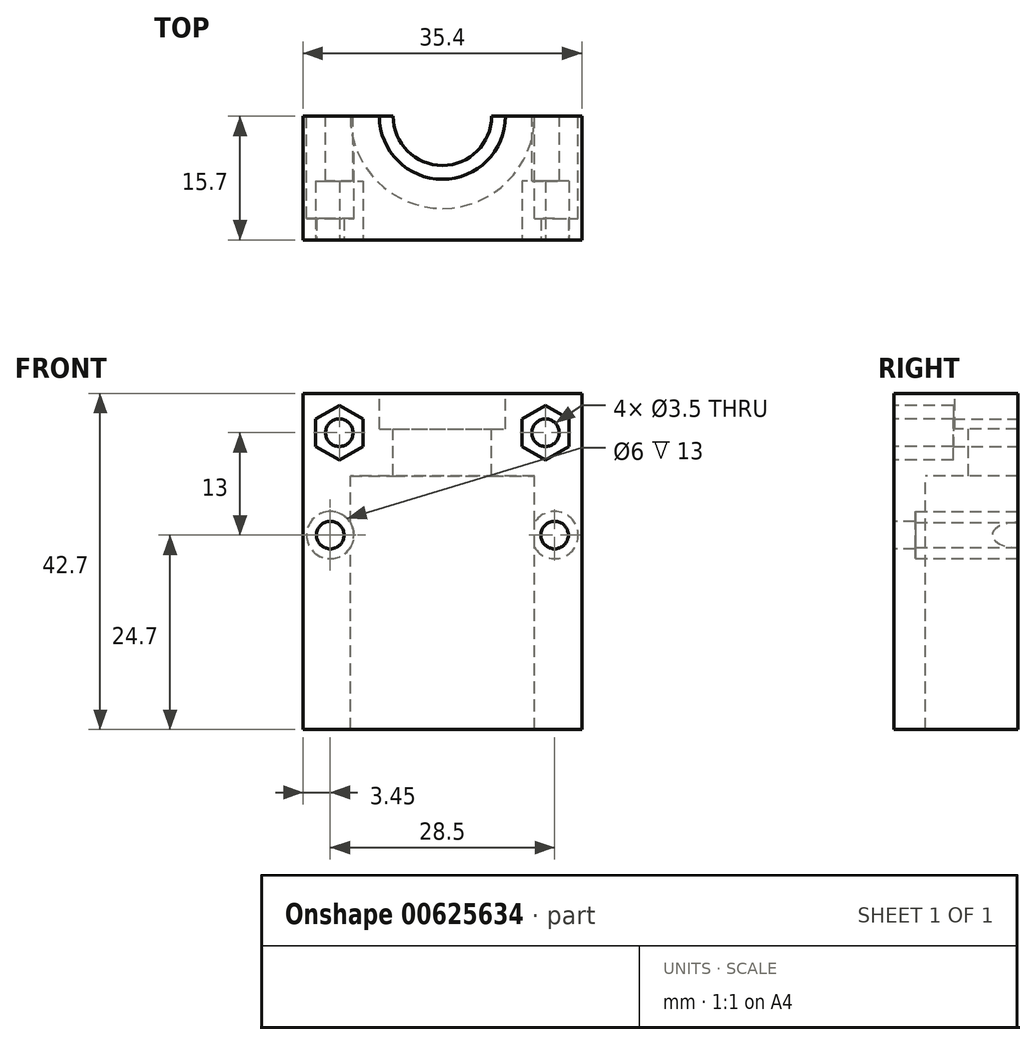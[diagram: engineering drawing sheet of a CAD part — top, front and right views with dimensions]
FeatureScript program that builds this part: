
annotation { "Feature Type Name" : "Feature", "Feature Type Description" : "" }
export const myFeature = defineFeature(function(context is Context, id is Id, definition is map)
    precondition{}
    {
        {
            var Q0;
            Q0=qCreatedBy(makeId("Top.planeOp"),FACE);
            var sketch = newSketch(context, id + "F0", { "sketchPlane" : qUnion([Q0])});
            skLineSegment(sketch, "E0.bottom", {"start": v(0, 0) * mm, "end": v(35.4, 0) * mm});
            skLineSegment(sketch, "E0.top", {"start": v(0, 15.7) * mm, "end": v(7.2, 15.7) * mm});
            skLineSegment(sketch, "E0.left", {"start": v(0, 0) * mm, "end": v(0, 15.7) * mm});
            skLineSegment(sketch, "E0.right", {"start": v(35.4, 0) * mm, "end": v(35.4, 15.7) * mm});
            skLineSegment(sketch, "E1.trimOffspring", {"start": v(23.2, 15.7) * mm, "end": v(35.4, 15.7) * mm});
            skLineSegment(sketch, "E2", {"start": v(7.2, 15.7) * mm, "end": v(23.2, 15.7) * mm});
            skSolve(sketch);
        }
        {
            var Q0;
            Q0=makeQuery(id+"F0.imprint","IMPRINT",FACE,{"disambiguationData":[TD([[makeQuery(id+"F0.imprint","IMPRINT",EDGE,{"derivedFrom":sQuery(id+"F0.wireOp",EDGE,"E0.bottom")}),1.0]])]});
            extrude(context, id + "F1", {"entities" : qUnion([Q0]), "depth" : 42.7 * mm, "offsetDistance" : 25 * mm});
        }
        {
            var Q0;
            Q0=makeQuery(id+"F1.opExtrude","CAP_FACE",FACE,{"disambiguationData":[OSD([sQuery(id+"F0.wireOp",EDGE,"E0.bottom"),sQuery(id+"F0.wireOp",EDGE,"E0.top"),sQuery(id+"F0.wireOp",EDGE,"E0.left"),sQuery(id+"F0.wireOp",EDGE,"E0.right"),sQuery(id+"F0.wireOp",EDGE,"E1.trimOffspring"),sQuery(id+"F0.wireOp",EDGE,"E2")])],"isStart":false});
            var sketch = newSketch(context, id + "F2", { "sketchPlane" : qUnion([Q0])});
            skCircle(sketch, "E3", {"center": v(17.7, 15.7) * mm, "radius": 8 * mm});
            skSolve(sketch);
        }
        {
            var Q0;
            {var subQ0=sQuery(id+"F2.wireOp",EDGE,"E3");var subQ1=makeQuery(id+"F1.opExtrude","CAP_EDGE",EDGE,{"disambiguationData":[OSD([sQuery(id+"F0.wireOp",EDGE,"E0.top"),sQuery(id+"F0.wireOp",EDGE,"E1.trimOffspring"),sQuery(id+"F0.wireOp",EDGE,"E2")])],"isStart":false});var subQ2=makeQuery(id+"F2.imprint","INTERSECT",VERTEX,{"disambiguationData":[OD(0.0)],"derivedFrom":[subQ1,subQ0]});Q0=makeQuery(id+"F2.imprint","IMPRINT",FACE,{"disambiguationData":[TD([[makeQuery(id+"F2.imprint","IMPRINT",EDGE,{"disambiguationData":[TD([[subQ2,-1.0]])],"derivedFrom":subQ0}),1.0]])]});}
            extrude(context, id + "F3", {"entities" : qUnion([Q0]), "operationType" : NewBodyOperationType.REMOVE, "oppositeDirection" : true, "depth" : 4.5 * mm, "offsetDistance" : 25 * mm});
        }
        {
            var Q0;
            Q0=makeQuery(id+"F3.boolean.opBoolean","COPY",FACE,{"derivedFrom":makeQuery(id+"F3.opExtrude","CAP_FACE",FACE,{"disambiguationData":[OSD([sQuery(id+"F0.wireOp",EDGE,"E0.top"),sQuery(id+"F0.wireOp",EDGE,"E1.trimOffspring"),sQuery(id+"F0.wireOp",EDGE,"E2"),sQuery(id+"F2.wireOp",EDGE,"E3")])],"isStart":false})});
            var sketch = newSketch(context, id + "F4", { "sketchPlane" : qUnion([Q0])});
            skPoint(sketch, "E4.center.orphan", {"position": v(17.7, 15.7) * mm});
            skCircle(sketch, "E5", {"center": v(17.7, 15.7) * mm, "radius": 6.25 * mm});
            skSolve(sketch);
        }
        {
            var Q0;
            {var subQ0=sQuery(id+"F4.wireOp",EDGE,"E5");var subQ1=makeQuery(id+"F3.boolean.opBoolean","COPY",EDGE,{"derivedFrom":makeQuery(id+"F3.opExtrude","CAP_EDGE",EDGE,{"disambiguationData":[OSD([sQuery(id+"F0.wireOp",EDGE,"E0.top"),sQuery(id+"F0.wireOp",EDGE,"E1.trimOffspring"),sQuery(id+"F0.wireOp",EDGE,"E2")])],"isStart":false})});var subQ2=makeQuery(id+"F4.imprint","INTERSECT",VERTEX,{"disambiguationData":[OD(0.0)],"derivedFrom":[subQ1,subQ0]});Q0=makeQuery(id+"F4.imprint","IMPRINT",FACE,{"disambiguationData":[TD([[makeQuery(id+"F4.imprint","IMPRINT",EDGE,{"disambiguationData":[TD([[subQ2,-1.0]])],"derivedFrom":subQ0}),1.0]])]});}
            extrude(context, id + "F5", {"entities" : qUnion([Q0]), "operationType" : NewBodyOperationType.REMOVE, "oppositeDirection" : true, "depth" : 6 * mm, "offsetDistance" : 25 * mm});
        }
        {
            var Q0;
            Q0=makeQuery(id+"F5.boolean.opBoolean","COPY",FACE,{"derivedFrom":makeQuery(id+"F5.opExtrude","CAP_FACE",FACE,{"disambiguationData":[OSD([sQuery(id+"F0.wireOp",EDGE,"E0.top"),sQuery(id+"F0.wireOp",EDGE,"E1.trimOffspring"),sQuery(id+"F0.wireOp",EDGE,"E2"),sQuery(id+"F4.wireOp",EDGE,"E5")])],"isStart":false})});
            var sketch = newSketch(context, id + "F6", { "sketchPlane" : qUnion([Q0])});
            skCircle(sketch, "E6", {"center": v(17.7, 15.7) * mm, "radius": 8 * mm});
            skSolve(sketch);
        }
        {
            var Q0;
            Q0 = qSketchRegion(id + "F6", true);
            extrude(context, id + "F7", {"entities" : qUnion([Q0]), "operationType" : NewBodyOperationType.REMOVE, "oppositeDirection" : true, "depth" : 50 * mm, "offsetDistance" : 25 * mm});
        }
        {
            var Q0;
            Q0=makeQuery(id+"F7.boolean.opBoolean","COPY",FACE,{"derivedFrom":makeQuery(id+"F7.opExtrude","CAP_FACE",FACE,{"disambiguationData":[OSD([sQuery(id+"F6.wireOp",EDGE,"E6")])],"isStart":true})});
            var sketch = newSketch(context, id + "F8", { "sketchPlane" : qUnion([Q0])});
            skCircle(sketch, "E7", {"center": v(17.7, -15.7) * mm, "radius": 11.7 * mm});
            skSolve(sketch);
        }
        {
            var Q0;
            Q0 = qSketchRegion(id + "F8", true);
            extrude(context, id + "F9", {"entities" : qUnion([Q0]), "operationType" : NewBodyOperationType.REMOVE, "depth" : 40 * mm, "offsetDistance" : 25 * mm});
        }
        {
            var Q0;
            Q0=makeQuery(id+"F1.opExtrude","SWEPT_FACE",FACE,{"disambiguationData":[OSD([sQuery(id+"F0.wireOp",EDGE,"E0.bottom")])]});
            var sketch = newSketch(context, id + "F10", { "sketchPlane" : qUnion([Q0])});
            skCircle(sketch, "E8", {"center": v(3.45, 24.7) * mm, "radius": 1.75 * mm});
            skCircle(sketch, "E9", {"center": v(31.95, 24.7) * mm, "radius": 1.75 * mm});
            skSolve(sketch);
        }
        {
            var Q0;
            Q0 = qSketchRegion(id + "F10", true);
            extrude(context, id + "F11", {"entities" : qUnion([Q0]), "operationType" : NewBodyOperationType.REMOVE, "oppositeDirection" : true, "depth" : 25 * mm, "offsetDistance" : 25 * mm});
        }
        {
            var Q0;
            {var subQ1=sQuery(id+"F0.wireOp",EDGE,"E0.right");var subQ2=sQuery(id+"F0.wireOp",EDGE,"E2");var subQ3=sQuery(id+"F0.wireOp",EDGE,"E1.trimOffspring");var subQ5=sQuery(id+"F0.wireOp",EDGE,"E0.top");Q0=makeQuery(id+"F7.boolean.opBoolean","SPLIT",FACE,{"disambiguationData":[TD([makeQuery(id+"F1.opExtrude","SWEPT_FACE",FACE,{"disambiguationData":[OSD([subQ1])]})])],"derivedFrom":makeQuery(id+"F1.opExtrude","SWEPT_FACE",FACE,{"disambiguationData":[OSD([subQ5,subQ3,subQ2])]})});}
            var sketch = newSketch(context, id + "F12", { "sketchPlane" : qUnion([Q0])});
            skCircle(sketch, "E10", {"center": v(-31.95, 24.7) * mm, "radius": 3 * mm});
            skSolve(sketch);
        }
        {
            var Q0;
            {var subQ2=sQuery(id+"F0.wireOp",EDGE,"E0.right");var subQ3=sQuery(id+"F0.wireOp",EDGE,"E2");var subQ4=sQuery(id+"F0.wireOp",EDGE,"E1.trimOffspring");var subQ6=sQuery(id+"F0.wireOp",EDGE,"E0.top");var subQ9=makeQuery(id+"F7.boolean.opBoolean","SPLIT",FACE,{"disambiguationData":[TD([makeQuery(id+"F1.opExtrude","SWEPT_FACE",FACE,{"disambiguationData":[OSD([subQ2])]})])],"derivedFrom":makeQuery(id+"F1.opExtrude","SWEPT_FACE",FACE,{"disambiguationData":[OSD([subQ6,subQ4,subQ3])]})});Q0=makeQuery(id+"F12.imprint","IMPRINT",FACE,{"disambiguationData":[TD([[makeQuery(id+"F12.imprint","IMPRINT",EDGE,{"derivedFrom":makeQuery(id+"F11.boolean.opBoolean","INTERSECT",EDGE,{"derivedFrom":[subQ9,makeQuery(id+"F11.opExtrude","SWEPT_FACE",FACE,{"disambiguationData":[OSD([sQuery(id+"F10.wireOp",EDGE,"E9")])]})]})}),-1.0]])]});}
            var Q1;
            {var subQ0=sQuery(id+"F12.wireOp",EDGE,"E10");var subQ2=sQuery(id+"F0.wireOp",EDGE,"E0.right");var subQ3=sQuery(id+"F0.wireOp",EDGE,"E2");var subQ4=sQuery(id+"F0.wireOp",EDGE,"E1.trimOffspring");var subQ6=sQuery(id+"F0.wireOp",EDGE,"E0.top");var subQ9=makeQuery(id+"F9.boolean.opBoolean","INTERSECT",EDGE,{"derivedFrom":[makeQuery(id+"F7.boolean.opBoolean","SPLIT",FACE,{"disambiguationData":[TD([makeQuery(id+"F1.opExtrude","SWEPT_FACE",FACE,{"disambiguationData":[OSD([subQ2])]})])],"derivedFrom":makeQuery(id+"F1.opExtrude","SWEPT_FACE",FACE,{"disambiguationData":[OSD([subQ6,subQ4,subQ3])]})}),makeQuery(id+"F9.opExtrude","SWEPT_FACE",FACE,{"disambiguationData":[OSD([sQuery(id+"F8.wireOp",EDGE,"E7")])]})]});var subQ10=makeQuery(id+"F12.imprint","INTERSECT",VERTEX,{"disambiguationData":[OD(0.0)],"derivedFrom":[subQ9,subQ0]});Q1=makeQuery(id+"F12.imprint","IMPRINT",FACE,{"disambiguationData":[TD([[makeQuery(id+"F12.imprint","IMPRINT",EDGE,{"disambiguationData":[TD([[subQ10,1.0]])],"derivedFrom":subQ0}),1.0]])]});}
            extrude(context, id + "F13", {"entities" : qUnion([Q0, Q1]), "operationType" : NewBodyOperationType.REMOVE, "oppositeDirection" : true, "depth" : 13 * mm, "offsetDistance" : 25 * mm});
        }
        {
            var Q0;
            {var subQ1=sQuery(id+"F0.wireOp",EDGE,"E0.left");var subQ2=sQuery(id+"F0.wireOp",EDGE,"E2");var subQ3=sQuery(id+"F0.wireOp",EDGE,"E1.trimOffspring");var subQ5=sQuery(id+"F0.wireOp",EDGE,"E0.top");Q0=makeQuery(id+"F7.boolean.opBoolean","SPLIT",FACE,{"disambiguationData":[TD([makeQuery(id+"F1.opExtrude","SWEPT_FACE",FACE,{"disambiguationData":[OSD([subQ1])]})])],"derivedFrom":makeQuery(id+"F1.opExtrude","SWEPT_FACE",FACE,{"disambiguationData":[OSD([subQ5,subQ3,subQ2])]})});}
            var sketch = newSketch(context, id + "F14", { "sketchPlane" : qUnion([Q0])});
            skCircle(sketch, "E11", {"center": v(-3.45, 24.7) * mm, "radius": 3 * mm});
            skSolve(sketch);
        }
        {
            var Q0;
            Q0=makeQuery(id+"F14.imprint","IMPRINT",FACE,{"disambiguationData":[TD([[makeQuery(id+"F14.imprint","IMPRINT",EDGE,{"derivedFrom":sQuery(id+"F14.wireOp",EDGE,"E11")}),1.0]])]});
            var Q1;
            {var subQ2=sQuery(id+"F0.wireOp",EDGE,"E0.left");var subQ3=sQuery(id+"F0.wireOp",EDGE,"E2");var subQ4=sQuery(id+"F0.wireOp",EDGE,"E1.trimOffspring");var subQ6=sQuery(id+"F0.wireOp",EDGE,"E0.top");var subQ9=makeQuery(id+"F7.boolean.opBoolean","SPLIT",FACE,{"disambiguationData":[TD([makeQuery(id+"F1.opExtrude","SWEPT_FACE",FACE,{"disambiguationData":[OSD([subQ2])]})])],"derivedFrom":makeQuery(id+"F1.opExtrude","SWEPT_FACE",FACE,{"disambiguationData":[OSD([subQ6,subQ4,subQ3])]})});Q1=makeQuery(id+"F14.imprint","IMPRINT",FACE,{"disambiguationData":[TD([[makeQuery(id+"F14.imprint","IMPRINT",EDGE,{"derivedFrom":makeQuery(id+"F11.boolean.opBoolean","INTERSECT",EDGE,{"derivedFrom":[subQ9,makeQuery(id+"F11.opExtrude","SWEPT_FACE",FACE,{"disambiguationData":[OSD([sQuery(id+"F10.wireOp",EDGE,"E8")])]})]})}),-1.0]])]});}
            extrude(context, id + "F15", {"entities" : qUnion([Q0, Q1]), "operationType" : NewBodyOperationType.REMOVE, "oppositeDirection" : true, "depth" : 13 * mm, "offsetDistance" : 25 * mm});
        }
        {
            var Q0;
            {var subQ1=sQuery(id+"F0.wireOp",EDGE,"E0.right");var subQ2=sQuery(id+"F0.wireOp",EDGE,"E2");var subQ3=sQuery(id+"F0.wireOp",EDGE,"E1.trimOffspring");var subQ5=sQuery(id+"F0.wireOp",EDGE,"E0.top");Q0=makeQuery(id+"F7.boolean.opBoolean","SPLIT",FACE,{"disambiguationData":[TD([makeQuery(id+"F1.opExtrude","SWEPT_FACE",FACE,{"disambiguationData":[OSD([subQ1])]})])],"derivedFrom":makeQuery(id+"F1.opExtrude","SWEPT_FACE",FACE,{"disambiguationData":[OSD([subQ5,subQ3,subQ2])]})});}
            var sketch = newSketch(context, id + "F16", { "sketchPlane" : qUnion([Q0])});
            skCircle(sketch, "E12", {"center": v(-30.8, 37.7) * mm, "radius": 1.75 * mm});
            skCircle(sketch, "E13", {"center": v(-4.6, 37.7) * mm, "radius": 1.75 * mm});
            skSolve(sketch);
        }
        {
            var Q0;
            Q0=makeQuery(id+"F16.imprint","IMPRINT",FACE,{"disambiguationData":[TD([[makeQuery(id+"F16.imprint","IMPRINT",EDGE,{"derivedFrom":sQuery(id+"F16.wireOp",EDGE,"E12")}),1.0]])]});
            var Q1;
            Q1=makeQuery(id+"F16.imprint","IMPRINT",FACE,{"disambiguationData":[TD([[makeQuery(id+"F16.imprint","IMPRINT",EDGE,{"derivedFrom":sQuery(id+"F16.wireOp",EDGE,"E13")}),1.0]])]});
            extrude(context, id + "F17", {"entities" : qUnion([Q0, Q1]), "operationType" : NewBodyOperationType.REMOVE, "oppositeDirection" : true, "depth" : 25 * mm, "offsetDistance" : 25 * mm});
        }
        {
            var Q0;
            Q0=makeQuery(id+"F1.opExtrude","SWEPT_FACE",FACE,{"disambiguationData":[OSD([sQuery(id+"F0.wireOp",EDGE,"E0.bottom")])]});
            var sketch = newSketch(context, id + "F18", { "sketchPlane" : qUnion([Q0])});
            skCircle(sketch, "E14.cCircle", {"center": v(4.6, 37.7) * mm, "radius": 3 * mm, "construction": true});
            skLineSegment(sketch, "E14.0", {"start": v(7.6, 39.43) * mm, "end": v(7.6, 35.97) * mm});
            skLineSegment(sketch, "E14.1", {"start": v(7.6, 35.97) * mm, "end": v(4.6, 34.24) * mm});
            skLineSegment(sketch, "E14.2", {"start": v(4.6, 34.24) * mm, "end": v(1.6, 35.97) * mm});
            skLineSegment(sketch, "E14.3", {"start": v(1.6, 35.97) * mm, "end": v(1.6, 39.43) * mm});
            skLineSegment(sketch, "E14.4", {"start": v(1.6, 39.43) * mm, "end": v(4.6, 41.16) * mm});
            skLineSegment(sketch, "E14.5", {"start": v(4.6, 41.16) * mm, "end": v(7.6, 39.43) * mm});
            skPoint(sketch, "E14.0.midPoint", {"position": v(7.6, 37.7) * mm});
            skCircle(sketch, "E15.cCircle", {"center": v(30.8, 37.7) * mm, "radius": 3 * mm, "construction": true});
            skLineSegment(sketch, "E15.0", {"start": v(27.8, 35.97) * mm, "end": v(27.8, 39.43) * mm});
            skLineSegment(sketch, "E15.1", {"start": v(27.8, 39.43) * mm, "end": v(30.8, 41.16) * mm});
            skLineSegment(sketch, "E15.2", {"start": v(30.8, 41.16) * mm, "end": v(33.8, 39.43) * mm});
            skLineSegment(sketch, "E15.3", {"start": v(33.8, 39.43) * mm, "end": v(33.8, 35.97) * mm});
            skLineSegment(sketch, "E15.4", {"start": v(33.8, 35.97) * mm, "end": v(30.8, 34.24) * mm});
            skLineSegment(sketch, "E15.5", {"start": v(30.8, 34.24) * mm, "end": v(27.8, 35.97) * mm});
            skPoint(sketch, "E15.0.midPoint", {"position": v(27.8, 37.7) * mm});
            skSolve(sketch);
        }
        {
            var Q0;
            Q0=makeQuery(id+"F18.imprint","IMPRINT",FACE,{"disambiguationData":[TD([[makeQuery(id+"F18.imprint","IMPRINT",EDGE,{"derivedFrom":sQuery(id+"F18.wireOp",EDGE,"E14.0")}),-1.0]])]});
            var Q1;
            Q1=makeQuery(id+"F18.imprint","IMPRINT",FACE,{"disambiguationData":[TD([[makeQuery(id+"F18.imprint","IMPRINT",EDGE,{"derivedFrom":sQuery(id+"F18.wireOp",EDGE,"E15.0")}),-1.0]])]});
            extrude(context, id + "F19", {"entities" : qUnion([Q0, Q1]), "operationType" : NewBodyOperationType.REMOVE, "oppositeDirection" : true, "depth" : 7.5 * mm, "offsetDistance" : 25 * mm});
        }
    });
